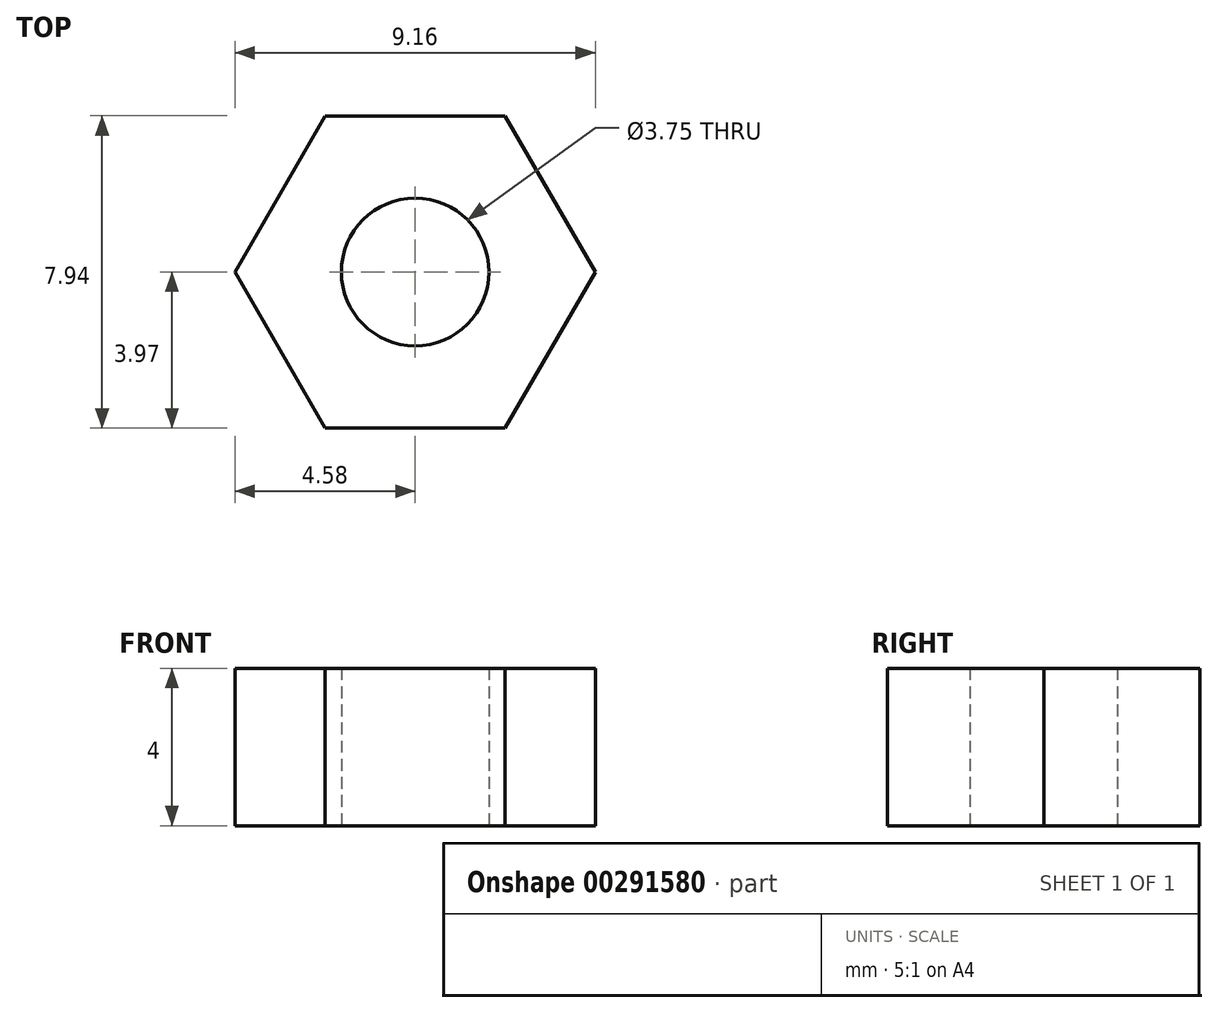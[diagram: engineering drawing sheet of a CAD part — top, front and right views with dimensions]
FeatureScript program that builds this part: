
annotation { "Feature Type Name" : "Feature", "Feature Type Description" : "" }
export const myFeature = defineFeature(function(context is Context, id is Id, definition is map)
    precondition{}
    {
        {
            var Q0;
            Q0=qCreatedBy(makeId("Top.planeOp"),FACE);
            var sketch = newSketch(context, id + "F0", { "sketchPlane" : qUnion([Q0])});
            skCircle(sketch, "E0.cCircle", {"center": v(0, 0) * mm, "radius": 3.96 * mm, "construction": true});
            skLineSegment(sketch, "E0.0", {"start": v(-2.29, 3.96) * mm, "end": v(2.29, 3.96) * mm});
            skLineSegment(sketch, "E0.1", {"start": v(2.29, 3.96) * mm, "end": v(4.58, 0) * mm});
            skLineSegment(sketch, "E0.2", {"start": v(4.58, 0) * mm, "end": v(2.29, -3.96) * mm});
            skLineSegment(sketch, "E0.3", {"start": v(2.29, -3.96) * mm, "end": v(-2.29, -3.97) * mm});
            skLineSegment(sketch, "E0.4", {"start": v(-2.29, -3.97) * mm, "end": v(-4.58, 0) * mm});
            skLineSegment(sketch, "E0.5", {"start": v(-4.58, 0) * mm, "end": v(-2.29, 3.96) * mm});
            skPoint(sketch, "E0.0.midPoint", {"position": v(0, 3.96) * mm});
            skCircle(sketch, "E1", {"center": v(0, 0) * mm, "radius": 1.88 * mm});
            skSolve(sketch);
        }
        {
            var Q0;
            Q0 = qSketchRegion(id + "F0", true);
            extrude(context, id + "F1", {"entities" : qUnion([Q0]), "depth" : 4 * mm});
        }
    });
